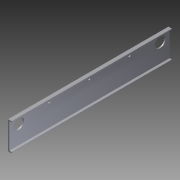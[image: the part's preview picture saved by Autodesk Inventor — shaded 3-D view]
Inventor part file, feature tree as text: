
AUTODESK INVENTOR PART (.ipt)
format: ipt  version: 2012 (Build 160160000, 160)  size: 107,008 bytes
history: native  units: in
note: dims shown in document units (in); Inventor stores cm internally (conversion verified against a paired STEP export)
features: extrude x2, sketch x2
ambient origin geometry x8: Origin, YZ Plane, XZ Plane, XY Plane, X Axis, Y Axis, Z Axis, Center Point
bodies: Solid1 (feature_tree)
feature tree (4):
  extrude  "Extrusion1"  Depth=0.125in
  extrude  "Extrusion2"  Depth=3.0in
  sketch  "Sketch1"  dims[d0=0.125in d2=0.125in]
  sketch  "Sketch2"  dims[d3=0.125in d4=3.0in d5=0.375in d6=17.25in d7=0.0in d8=1.125in d10=2.125in d11=1.0in d12=20.0in d13=0.0in d14=1.0in d15=2.125in d16=1.125in d17=0.25in d18=0.5in d19=8.625in d20=4.3125in d21=4.3125in d22=0.25in d23=0.25in d24=17.25in]
